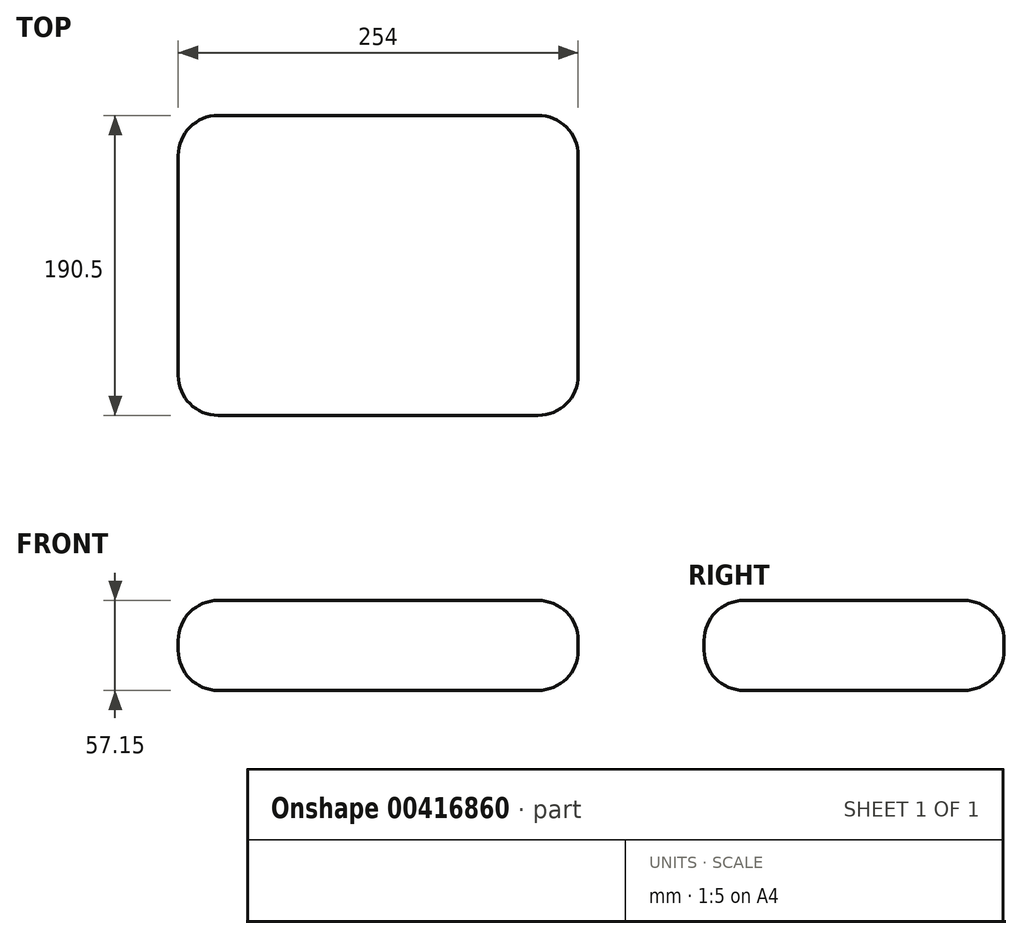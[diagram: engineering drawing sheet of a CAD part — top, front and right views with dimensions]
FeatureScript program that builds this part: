
annotation { "Feature Type Name" : "Feature", "Feature Type Description" : "" }
export const myFeature = defineFeature(function(context is Context, id is Id, definition is map)
    precondition{}
    {
        {
            var Q0;
            Q0=qCreatedBy(makeId("Top.planeOp"),FACE);
            var sketch = newSketch(context, id + "F0", { "sketchPlane" : qUnion([Q0])});
            skLineSegment(sketch, "E0.bottom", {"start": v(-127, 95.25) * mm, "end": v(127, 95.25) * mm});
            skLineSegment(sketch, "E0.top", {"start": v(-127, -95.25) * mm, "end": v(127, -95.25) * mm});
            skLineSegment(sketch, "E0.left", {"start": v(-127, 95.25) * mm, "end": v(-127, -95.25) * mm});
            skLineSegment(sketch, "E0.right", {"start": v(127, 95.25) * mm, "end": v(127, -95.25) * mm});
            skPoint(sketch, "E0.middle", {"position": v(0, 0) * mm});
            skSolve(sketch);
        }
        {
            var Q0;
            Q0 = qSketchRegion(id + "F0", true);
            extrude(context, id + "F1", {"entities" : qUnion([Q0]), "depth" : 57.15 * mm});
        }
        {
            var Q0;
            Q0=makeQuery(id+"F1.opExtrude","SWEPT_FACE",FACE,{"disambiguationData":[OSD([sQuery(id+"F0.wireOp",EDGE,"E0.left")])]});
            var Q1;
            Q1=makeQuery(id+"F1.opExtrude","SWEPT_FACE",FACE,{"disambiguationData":[OSD([sQuery(id+"F0.wireOp",EDGE,"E0.top")])]});
            var Q2;
            Q2=makeQuery(id+"F1.opExtrude","SWEPT_FACE",FACE,{"disambiguationData":[OSD([sQuery(id+"F0.wireOp",EDGE,"E0.right")])]});
            var Q3;
            Q3=makeQuery(id+"F1.opExtrude","SWEPT_FACE",FACE,{"disambiguationData":[OSD([sQuery(id+"F0.wireOp",EDGE,"E0.bottom")])]});
            fillet(context, id + "F2", {"entities" : qUnion([Q0, Q1, Q2, Q3]), "radius" : 25.4 * mm, "tangentPropagation" : true, "allowEdgeOverflow" : false});
        }
    });
